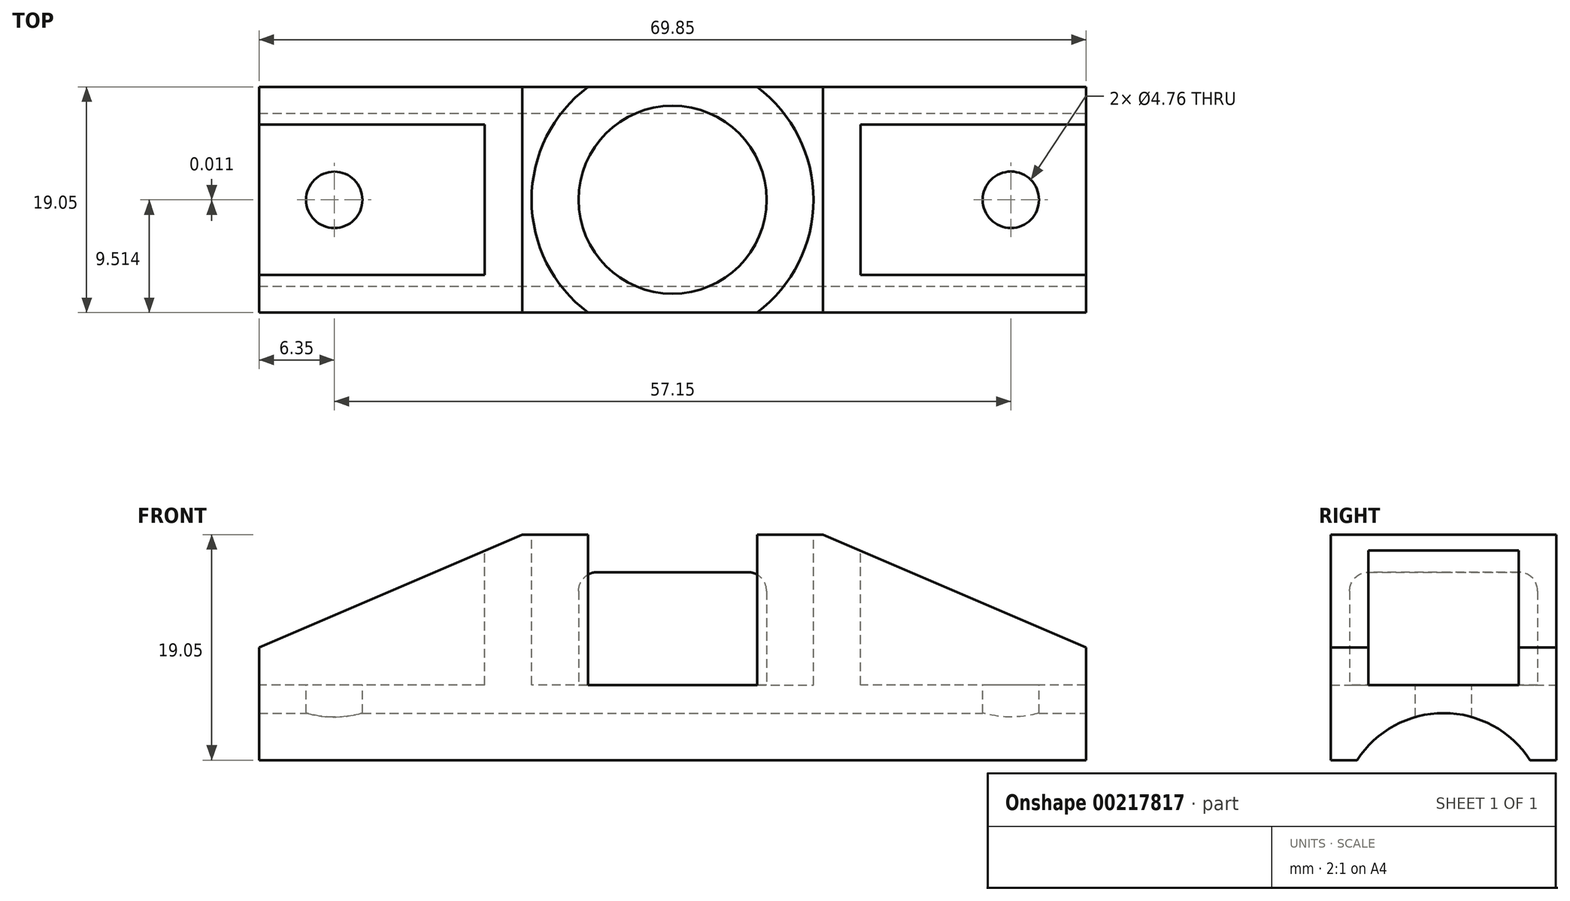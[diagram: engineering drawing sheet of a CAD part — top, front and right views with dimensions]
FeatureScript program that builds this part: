
annotation { "Feature Type Name" : "Feature", "Feature Type Description" : "" }
export const myFeature = defineFeature(function(context is Context, id is Id, definition is map)
    precondition{}
    {
        {
            var Q0;
            Q0=qCreatedBy(makeId("Top.planeOp"),FACE);
            var sketch = newSketch(context, id + "F0", { "sketchPlane" : qUnion([Q0])});
            skLineSegment(sketch, "E0.bottom", {"start": v(0, 0) * mm, "end": v(69.85, 0) * mm});
            skLineSegment(sketch, "E0.top", {"start": v(0, 19.05) * mm, "end": v(69.85, 19.05) * mm});
            skLineSegment(sketch, "E0.left", {"start": v(0, 0) * mm, "end": v(0, 19.05) * mm});
            skLineSegment(sketch, "E0.right", {"start": v(69.85, 0) * mm, "end": v(69.85, 19.05) * mm});
            skSolve(sketch);
        }
        {
            var Q0;
            Q0 = qSketchRegion(id + "F0", true);
            extrude(context, id + "F1", {"entities" : qUnion([Q0]), "depth" : 19.05 * mm});
        }
        {
            var Q0;
            Q0=makeQuery(id+"F1.opExtrude","CAP_FACE",FACE,{"disambiguationData":[OSD([sQuery(id+"F0.wireOp",EDGE,"E0.bottom"),sQuery(id+"F0.wireOp",EDGE,"E0.top"),sQuery(id+"F0.wireOp",EDGE,"E0.left"),sQuery(id+"F0.wireOp",EDGE,"E0.right")])],"isStart":false});
            var sketch = newSketch(context, id + "F2", { "sketchPlane" : qUnion([Q0])});
            skCircle(sketch, "E1", {"center": v(34.92, 9.53) * mm, "radius": 11.9 * mm});
            skPoint(sketch, "E1.centerSnap0", {"position": v(0, 9.53) * mm});
            skPoint(sketch, "E1.centerSnap1", {"position": v(34.92, 0) * mm});
            skSolve(sketch);
        }
        {
            var Q0;
            Q0 = qSketchRegion(id + "F2", true);
            extrude(context, id + "F3", {"entities" : qUnion([Q0]), "operationType" : NewBodyOperationType.REMOVE, "oppositeDirection" : true, "depth" : 12.7 * mm});
        }
        {
            var Q0;
            Q0=makeQuery(id+"F3.boolean.opBoolean","COPY",FACE,{"derivedFrom":makeQuery(id+"F3.opExtrude","CAP_FACE",FACE,{"disambiguationData":[OSD([sQuery(id+"F2.wireOp",EDGE,"E1")])],"isStart":false})});
            var sketch = newSketch(context, id + "F4", { "sketchPlane" : qUnion([Q0])});
            skCircle(sketch, "E2", {"center": v(34.92, 9.53) * mm, "radius": 7.94 * mm});
            skSolve(sketch);
        }
        {
            var Q0;
            Q0 = qSketchRegion(id + "F4", true);
            extrude(context, id + "F5", {"entities" : qUnion([Q0]), "operationType" : NewBodyOperationType.ADD, "depth" : 9.52 * mm});
        }
        {
            var Q0;
            {var subQ0=sQuery(id+"F0.wireOp",EDGE,"E0.bottom");var subQ1=sQuery(id+"F0.wireOp",EDGE,"E0.top");var subQ2=sQuery(id+"F0.wireOp",EDGE,"E0.right");Q0=makeQuery(id+"F3.boolean.opBoolean","SPLIT",FACE,{"disambiguationData":[TD([makeQuery(id+"F1.opExtrude","SWEPT_FACE",FACE,{"disambiguationData":[OSD([subQ2])]})])],"derivedFrom":makeQuery(id+"F1.opExtrude","CAP_FACE",FACE,{"disambiguationData":[OSD([subQ0,subQ1,sQuery(id+"F0.wireOp",EDGE,"E0.left"),subQ2])],"isStart":false})});}
            var sketch = newSketch(context, id + "F6", { "sketchPlane" : qUnion([Q0])});
            skLineSegment(sketch, "E3.bottom", {"start": v(88.9, 15.88) * mm, "end": v(50.8, 15.88) * mm});
            skLineSegment(sketch, "E3.top", {"start": v(88.9, 3.18) * mm, "end": v(50.8, 3.18) * mm});
            skLineSegment(sketch, "E3.left", {"start": v(88.9, 15.88) * mm, "end": v(88.9, 3.18) * mm});
            skLineSegment(sketch, "E3.right", {"start": v(50.8, 15.88) * mm, "end": v(50.8, 3.18) * mm});
            skPoint(sketch, "E3.middle", {"position": v(69.85, 9.52) * mm});
            skLineSegment(sketch, "E4.1.0.0", {"start": v(19.05, 15.88) * mm, "end": v(-19.05, 15.88) * mm});
            skLineSegment(sketch, "E4.1.0.1", {"start": v(19.05, 15.88) * mm, "end": v(19.05, 3.18) * mm});
            skLineSegment(sketch, "E4.1.0.2", {"start": v(19.05, 3.18) * mm, "end": v(-19.05, 3.18) * mm});
            skLineSegment(sketch, "E4.1.0.3", {"start": v(-19.05, 15.88) * mm, "end": v(-19.05, 3.18) * mm});
            skLineSegment(sketch, "E4.direction1", {"start": v(50.8, 15.88) * mm, "end": v(-19.05, 15.88) * mm, "construction": true});
            skSolve(sketch);
        }
        {
            var Q0;
            Q0 = qSketchRegion(id + "F6", true);
            extrude(context, id + "F7", {"entities" : qUnion([Q0]), "operationType" : NewBodyOperationType.REMOVE, "oppositeDirection" : true, "depth" : 12.7 * mm});
        }
        {
            var Q0;
            Q0=makeQuery(id+"F7.boolean.opBoolean","COPY",FACE,{"derivedFrom":makeQuery(id+"F7.opExtrude","CAP_FACE",FACE,{"disambiguationData":[OSD([sQuery(id+"F6.wireOp",EDGE,"E3.bottom"),sQuery(id+"F6.wireOp",EDGE,"E3.top"),sQuery(id+"F6.wireOp",EDGE,"E3.left"),sQuery(id+"F6.wireOp",EDGE,"E3.right")])],"isStart":false})});
            var sketch = newSketch(context, id + "F8", { "sketchPlane" : qUnion([Q0])});
            skLineSegment(sketch, "E5", {"start": v(69.85, 9.53) * mm, "end": v(-10.46, 9.53) * mm, "construction": true});
            skCircle(sketch, "E6", {"center": v(63.5, 9.53) * mm, "radius": 2.38 * mm});
            skCircle(sketch, "E7", {"center": v(6.35, 9.51) * mm, "radius": 2.38 * mm});
            skSolve(sketch);
        }
        {
            var Q0;
            Q0 = qSketchRegion(id + "F8", true);
            extrude(context, id + "F9", {"entities" : qUnion([Q0]), "operationType" : NewBodyOperationType.REMOVE, "oppositeDirection" : true, "depth" : 25.4 * mm});
        }
        {
            var Q0;
            Q0=makeQuery(id+"F1.opExtrude","SWEPT_FACE",FACE,{"disambiguationData":[OSD([sQuery(id+"F0.wireOp",EDGE,"E0.right")])]});
            var sketch = newSketch(context, id + "F10", { "sketchPlane" : qUnion([Q0])});
            skLineSegment(sketch, "E8", {"start": v(9.52, 6.35) * mm, "end": v(9.52, -15.8) * mm, "construction": true});
            skCircle(sketch, "E9", {"center": v(9.52, -4.73) * mm, "radius": 8.7 * mm});
            skSolve(sketch);
        }
        {
            var Q0;
            Q0 = qSketchRegion(id + "F10", true);
            extrude(context, id + "F11", {"entities" : qUnion([Q0]), "operationType" : NewBodyOperationType.REMOVE, "endBound" : BoundingType.THROUGH_ALL, "oppositeDirection" : true, "depth" : 25.4 * mm});
        }
        {
            var Q0;
            Q0=makeQuery(id+"F5.opExtrude","CAP_EDGE",EDGE,{"disambiguationData":[OSD([sQuery(id+"F4.wireOp",EDGE,"E2")])],"isStart":false});
            fillet(context, id + "F12", {"entities" : qUnion([Q0]), "radius" : 1.59 * mm, "tangentPropagation" : true, "allowEdgeOverflow" : false});
        }
        {
            var Q0;
            {var subQ0=sQuery(id+"F0.wireOp",EDGE,"E0.bottom");var subQ1=sQuery(id+"F0.wireOp",EDGE,"E0.left");Q0=makeQuery(id+"F7.boolean.opBoolean","SPLIT",EDGE,{"disambiguationData":[TD([makeQuery(id+"F1.opExtrude","SWEPT_FACE",FACE,{"disambiguationData":[OSD([subQ0])]})])],"derivedFrom":makeQuery(id+"F1.opExtrude","CAP_EDGE",EDGE,{"disambiguationData":[OSD([subQ1])],"isStart":false})});}
            var Q1;
            {var subQ0=sQuery(id+"F0.wireOp",EDGE,"E0.left");var subQ1=sQuery(id+"F0.wireOp",EDGE,"E0.top");Q1=makeQuery(id+"F7.boolean.opBoolean","SPLIT",EDGE,{"disambiguationData":[TD([makeQuery(id+"F1.opExtrude","SWEPT_FACE",FACE,{"disambiguationData":[OSD([subQ1])]})])],"derivedFrom":makeQuery(id+"F1.opExtrude","CAP_EDGE",EDGE,{"disambiguationData":[OSD([subQ0])],"isStart":false})});}
            chamfer(context, id + "F13", {"entities" : qUnion([Q0, Q1]), "chamferType" : ChamferType.TWO_OFFSETS, "width1" : 9.52 * mm, "oppositeDirection" : false, "width2" : 22.22 * mm, "tangentPropagation" : true});
        }
        {
            var Q0;
            {var subQ0=sQuery(id+"F0.wireOp",EDGE,"E0.right");var subQ1=sQuery(id+"F0.wireOp",EDGE,"E0.top");Q0=makeQuery(id+"F7.boolean.opBoolean","SPLIT",EDGE,{"disambiguationData":[TD([makeQuery(id+"F1.opExtrude","SWEPT_FACE",FACE,{"disambiguationData":[OSD([subQ1])]})])],"derivedFrom":makeQuery(id+"F1.opExtrude","CAP_EDGE",EDGE,{"disambiguationData":[OSD([subQ0])],"isStart":false})});}
            var Q1;
            {var subQ0=sQuery(id+"F0.wireOp",EDGE,"E0.bottom");var subQ1=sQuery(id+"F0.wireOp",EDGE,"E0.right");Q1=makeQuery(id+"F7.boolean.opBoolean","SPLIT",EDGE,{"disambiguationData":[TD([makeQuery(id+"F1.opExtrude","SWEPT_FACE",FACE,{"disambiguationData":[OSD([subQ0])]})])],"derivedFrom":makeQuery(id+"F1.opExtrude","CAP_EDGE",EDGE,{"disambiguationData":[OSD([subQ1])],"isStart":false})});}
            chamfer(context, id + "F14", {"entities" : qUnion([Q0, Q1]), "chamferType" : ChamferType.TWO_OFFSETS, "width1" : 22.22 * mm, "oppositeDirection" : false, "width2" : 9.52 * mm, "tangentPropagation" : true});
        }
    });
